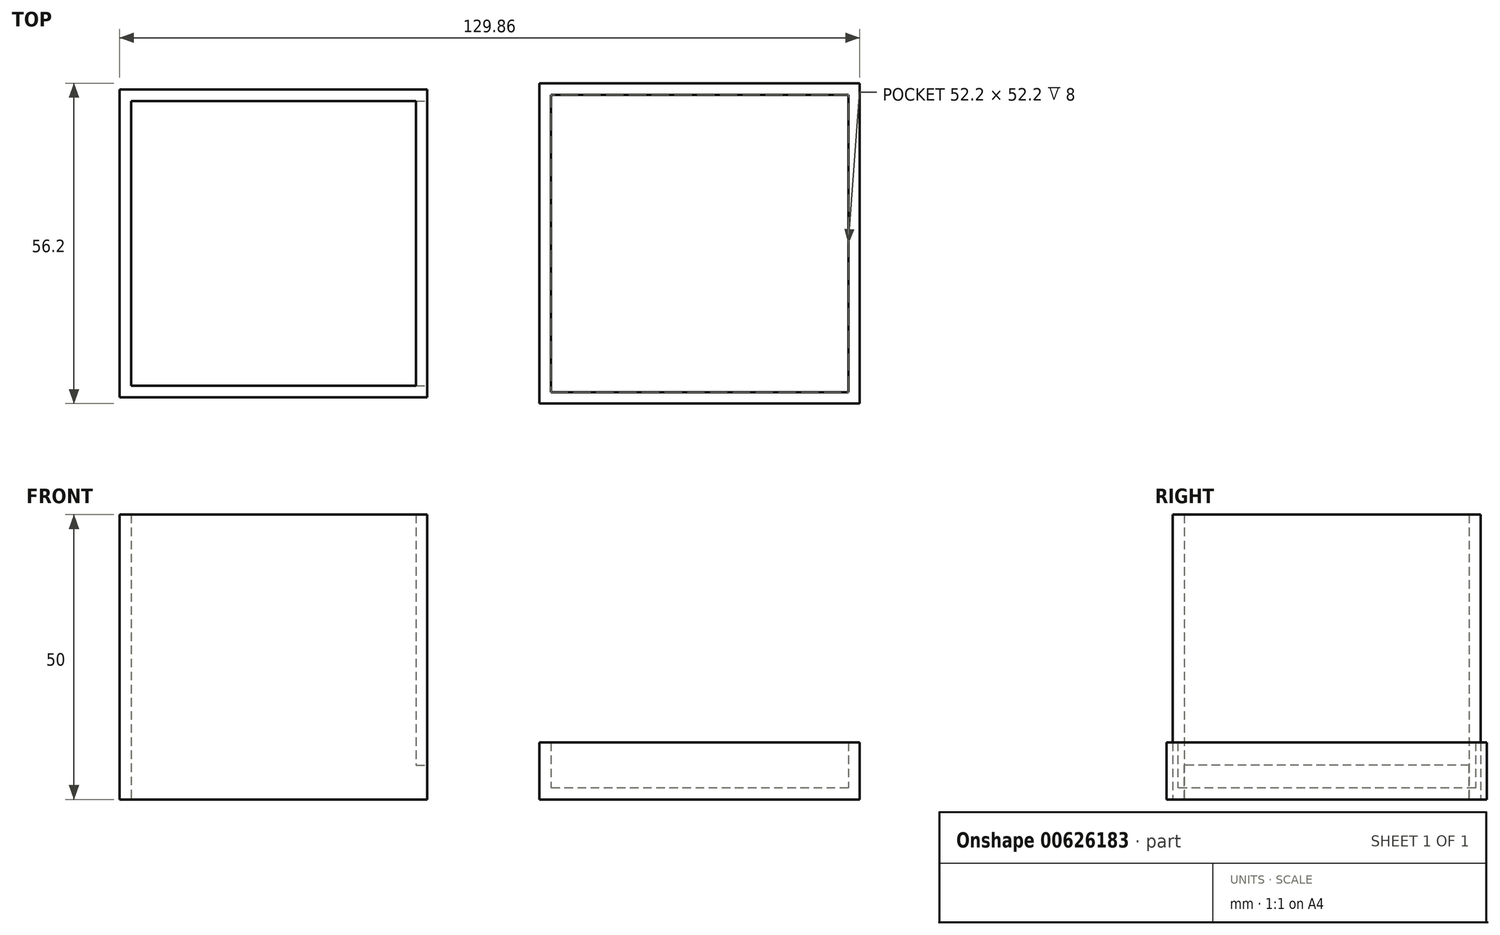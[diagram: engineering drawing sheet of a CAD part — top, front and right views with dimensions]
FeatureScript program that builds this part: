
annotation { "Feature Type Name" : "Feature", "Feature Type Description" : "" }
export const myFeature = defineFeature(function(context is Context, id is Id, definition is map)
    precondition{}
    {
        {
            var Q0;
            Q0=qCreatedBy(makeId("Top.planeOp"),FACE);
            var sketch = newSketch(context, id + "F0", { "sketchPlane" : qUnion([Q0])});
            skLineSegment(sketch, "E0.bottom", {"start": v(25, -25) * mm, "end": v(-25, -25) * mm});
            skLineSegment(sketch, "E0.top", {"start": v(25, 25) * mm, "end": v(-25, 25) * mm});
            skLineSegment(sketch, "E0.left", {"start": v(25, -25) * mm, "end": v(25, 25) * mm});
            skLineSegment(sketch, "E0.right", {"start": v(-25, -25) * mm, "end": v(-25, 25) * mm});
            skPoint(sketch, "E0.middle", {"position": v(0, 0) * mm});
            skLineSegment(sketch, "E1.0", {"start": v(27, 27) * mm, "end": v(-27, 27) * mm});
            skLineSegment(sketch, "E1.1", {"start": v(27, -27) * mm, "end": v(27, 27) * mm});
            skLineSegment(sketch, "E1.2", {"start": v(27, -27) * mm, "end": v(-27, -27) * mm});
            skLineSegment(sketch, "E1.3", {"start": v(-27, -27) * mm, "end": v(-27, 27) * mm});
            skLineSegment(sketch, "E2.bottom", {"start": v(100.86, 26.1) * mm, "end": v(48.66, 26.1) * mm});
            skLineSegment(sketch, "E2.top", {"start": v(100.86, -26.1) * mm, "end": v(48.66, -26.1) * mm});
            skLineSegment(sketch, "E2.left", {"start": v(100.86, 26.1) * mm, "end": v(100.86, -26.1) * mm});
            skLineSegment(sketch, "E2.right", {"start": v(48.66, 26.1) * mm, "end": v(48.66, -26.1) * mm});
            skPoint(sketch, "E2.middle", {"position": v(74.76, 0) * mm});
            skLineSegment(sketch, "E3.0", {"start": v(102.86, 28.1) * mm, "end": v(46.66, 28.1) * mm});
            skLineSegment(sketch, "E3.1", {"start": v(102.86, 28.1) * mm, "end": v(102.86, -28.1) * mm});
            skLineSegment(sketch, "E3.2", {"start": v(102.86, -28.1) * mm, "end": v(46.66, -28.1) * mm});
            skLineSegment(sketch, "E3.3", {"start": v(46.66, 28.1) * mm, "end": v(46.66, -28.1) * mm});
            skSolve(sketch);
        }
        {
            var Q0;
            Q0=makeQuery(id+"F0.imprint","IMPRINT",FACE,{"disambiguationData":[TD([[makeQuery(id+"F0.imprint","IMPRINT",EDGE,{"derivedFrom":sQuery(id+"F0.wireOp",EDGE,"E0.bottom")}),1.0]])]});
            extrude(context, id + "F1", {"entities" : qUnion([Q0]), "depth" : 50 * mm, "offsetDistance" : 25 * mm});
        }
        {
            var Q0;
            Q0=qCreatedBy(makeId("Right.planeOp"),FACE);
            cPlane(context, id + "F2", {"entities" : qUnion([Q0]), "cplaneType" : CPlaneType.OFFSET, "offset" : 27 * mm, "width" : 150 * mm, "height" : 150 * mm});
        }
        {
            var Q0;
            Q0=qCreatedBy(id+"F2.planeOp",FACE);
            var sketch = newSketch(context, id + "F3", { "sketchPlane" : qUnion([Q0])});
            skLineSegment(sketch, "E4.bottom", {"start": v(25, 0) * mm, "end": v(-25, 0) * mm});
            skLineSegment(sketch, "E4.top", {"start": v(25, 6) * mm, "end": v(-25, 6) * mm});
            skLineSegment(sketch, "E4.left", {"start": v(25, 0) * mm, "end": v(25, 6) * mm});
            skLineSegment(sketch, "E4.right", {"start": v(-25, 0) * mm, "end": v(-25, 6) * mm});
            skSolve(sketch);
        }
        {
            var Q0;
            Q0=makeQuery(id+"F3.imprint","IMPRINT",FACE,{"disambiguationData":[TD([[makeQuery(id+"F3.imprint","IMPRINT",EDGE,{"derivedFrom":sQuery(id+"F3.wireOp",EDGE,"E4.bottom")}),-1.0]])]});
            extrude(context, id + "F4", {"entities" : qUnion([Q0]), "operationType" : NewBodyOperationType.REMOVE, "oppositeDirection" : true, "depth" : 2 * mm, "offsetDistance" : 25 * mm});
        }
        {
            var Q0;
            Q0=makeQuery(id+"F0.imprint","IMPRINT",FACE,{"disambiguationData":[TD([[makeQuery(id+"F0.imprint","IMPRINT",EDGE,{"derivedFrom":sQuery(id+"F0.wireOp",EDGE,"E2.bottom")}),-1.0]])]});
            extrude(context, id + "F5", {"entities" : qUnion([Q0]), "depth" : 10 * mm, "offsetDistance" : 25 * mm});
        }
        {
            var Q0;
            Q0=makeQuery(id+"F0.imprint","IMPRINT",FACE,{"disambiguationData":[TD([[makeQuery(id+"F0.imprint","IMPRINT",EDGE,{"derivedFrom":sQuery(id+"F0.wireOp",EDGE,"E2.bottom")}),1.0]])]});
            extrude(context, id + "F6", {"entities" : qUnion([Q0]), "operationType" : NewBodyOperationType.ADD, "depth" : 2 * mm, "offsetDistance" : 25 * mm});
        }
    });
